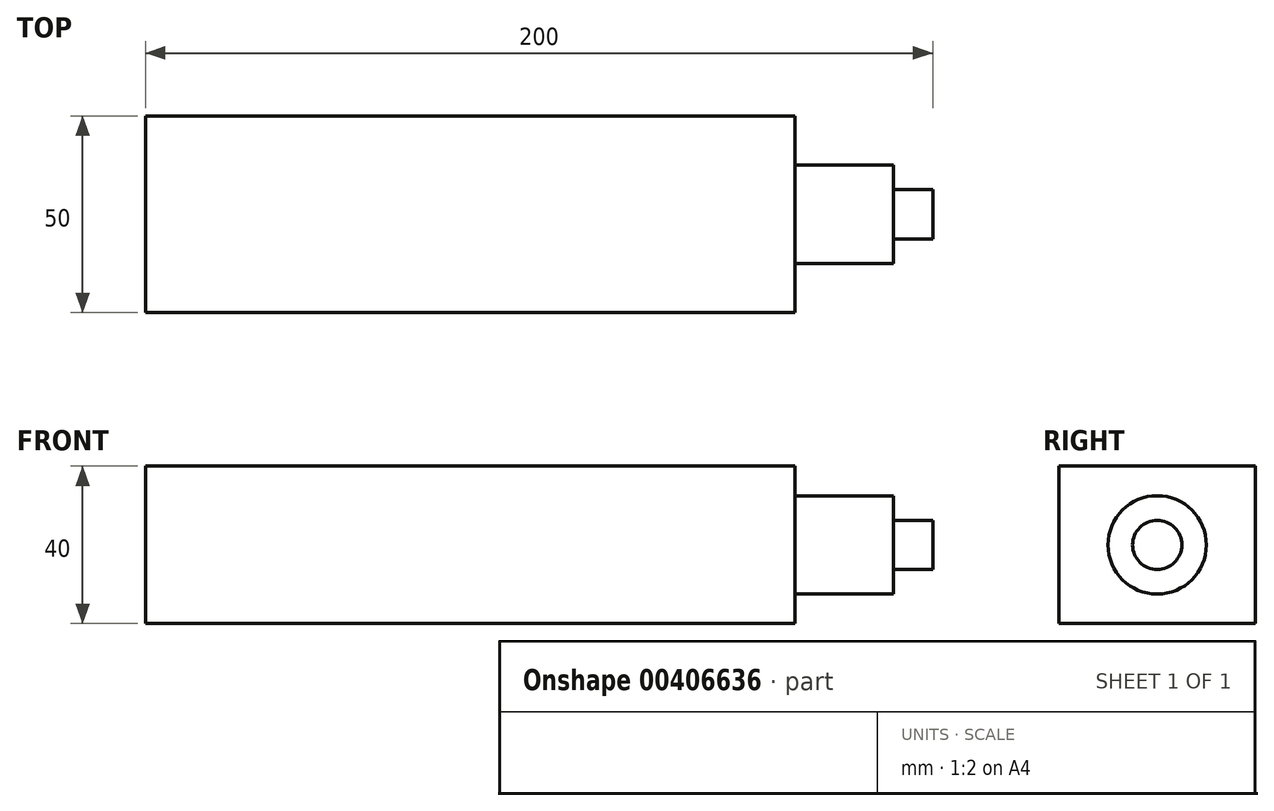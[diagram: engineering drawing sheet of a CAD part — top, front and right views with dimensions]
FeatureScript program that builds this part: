
annotation { "Feature Type Name" : "Feature", "Feature Type Description" : "" }
export const myFeature = defineFeature(function(context is Context, id is Id, definition is map)
    precondition{}
    {
        {
            var Q0;
            Q0=qCreatedBy(makeId("Top.planeOp"),FACE);
            var sketch = newSketch(context, id + "F0", { "sketchPlane" : qUnion([Q0])});
            skLineSegment(sketch, "E0.bottom", {"start": v(82.5, -25) * mm, "end": v(-82.5, -25) * mm});
            skLineSegment(sketch, "E0.top", {"start": v(82.5, 25) * mm, "end": v(-82.5, 25) * mm});
            skLineSegment(sketch, "E0.left", {"start": v(82.5, -25) * mm, "end": v(82.5, 25) * mm});
            skLineSegment(sketch, "E0.right", {"start": v(-82.5, -25) * mm, "end": v(-82.5, 25) * mm});
            skPoint(sketch, "E0.middle", {"position": v(0, 0) * mm});
            skSolve(sketch);
        }
        {
            var Q0;
            Q0=makeQuery(id+"F0.imprint","IMPRINT",FACE,{"disambiguationData":[TD([[makeQuery(id+"F0.imprint","IMPRINT",EDGE,{"derivedFrom":sQuery(id+"F0.wireOp",EDGE,"E0.bottom")}),-1.0]])]});
            extrude(context, id + "F1", {"entities" : qUnion([Q0]), "depth" : 40 * mm});
        }
        {
            var Q0;
            Q0=makeQuery(id+"F1.opExtrude","SWEPT_FACE",FACE,{"disambiguationData":[OSD([sQuery(id+"F0.wireOp",EDGE,"E0.left")])]});
            var sketch = newSketch(context, id + "F2", { "sketchPlane" : qUnion([Q0])});
            skCircle(sketch, "E1", {"center": v(0, 20) * mm, "radius": 12.5 * mm});
            skPoint(sketch, "E1.centerSnap0", {"position": v(-25, 20) * mm});
            skPoint(sketch, "E1.centerSnap1", {"position": v(0, 0) * mm});
            skSolve(sketch);
        }
        {
            var Q0;
            Q0 = qSketchRegion(id + "F2", true);
            extrude(context, id + "F3", {"entities" : qUnion([Q0]), "operationType" : NewBodyOperationType.ADD, "depth" : 25 * mm});
        }
        {
            var Q0;
            Q0=makeQuery(id+"F3.opExtrude","CAP_FACE",FACE,{"disambiguationData":[OSD([sQuery(id+"F2.wireOp",EDGE,"E1")])],"isStart":false});
            var sketch = newSketch(context, id + "F4", { "sketchPlane" : qUnion([Q0])});
            skCircle(sketch, "E2", {"center": v(0, 20) * mm, "radius": 6.25 * mm});
            skSolve(sketch);
        }
        {
            var Q0;
            Q0 = qSketchRegion(id + "F4", true);
            extrude(context, id + "F5", {"entities" : qUnion([Q0]), "operationType" : NewBodyOperationType.ADD, "depth" : 10 * mm});
        }
    });
